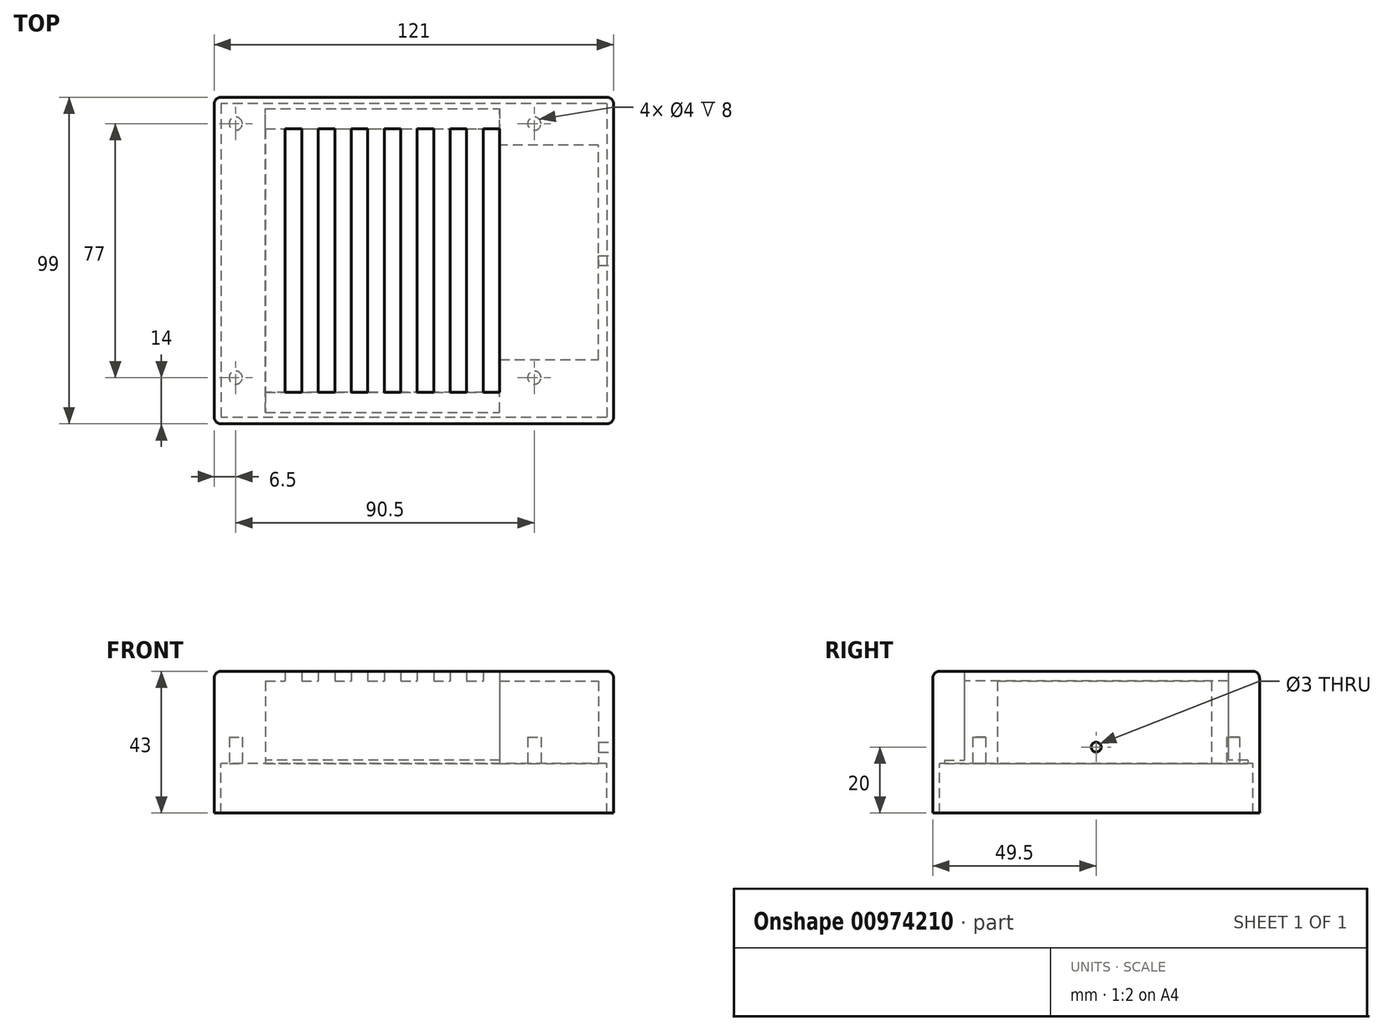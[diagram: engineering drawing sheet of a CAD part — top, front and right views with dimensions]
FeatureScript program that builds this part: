
annotation { "Feature Type Name" : "Feature", "Feature Type Description" : "" }
export const myFeature = defineFeature(function(context is Context, id is Id, definition is map)
    precondition{}
    {
        {
            var Q0;
            Q0=qCreatedBy(makeId("Top.planeOp"),FACE);
            var sketch = newSketch(context, id + "F0", { "sketchPlane" : qUnion([Q0])});
            skLineSegment(sketch, "E0.bottom", {"start": v(58.5, 47.5) * mm, "end": v(-58.5, 47.5) * mm});
            skLineSegment(sketch, "E0.top", {"start": v(58.5, -47.5) * mm, "end": v(-58.5, -47.5) * mm});
            skLineSegment(sketch, "E0.left", {"start": v(58.5, 47.5) * mm, "end": v(58.5, -47.5) * mm});
            skLineSegment(sketch, "E0.right", {"start": v(-58.5, 47.5) * mm, "end": v(-58.5, -47.5) * mm});
            skPoint(sketch, "E0.middle", {"position": v(0, 0) * mm});
            skLineSegment(sketch, "E1.bottom", {"start": v(60.5, 49.5) * mm, "end": v(-60.5, 49.5) * mm});
            skLineSegment(sketch, "E1.top", {"start": v(60.5, -49.5) * mm, "end": v(-60.5, -49.5) * mm});
            skLineSegment(sketch, "E1.left", {"start": v(60.5, 49.5) * mm, "end": v(60.5, -49.5) * mm});
            skLineSegment(sketch, "E1.right", {"start": v(-60.5, 49.5) * mm, "end": v(-60.5, -49.5) * mm});
            skSolve(sketch);
        }
        {
            var Q0;
            Q0=makeQuery(id+"F0.imprint","IMPRINT",FACE,{"disambiguationData":[TD([[makeQuery(id+"F0.imprint","IMPRINT",EDGE,{"derivedFrom":sQuery(id+"F0.wireOp",EDGE,"E0.bottom")}),-1.0]])]});
            extrude(context, id + "F1", {"entities" : qUnion([Q0]), "oppositeDirection" : true, "depth" : 15 * mm, "offsetDistance" : 25 * mm});
        }
        {
            var Q0;
            Q0=makeQuery(id+"F1.opExtrude","CAP_FACE",FACE,{"disambiguationData":[OSD([sQuery(id+"F0.wireOp",EDGE,"E0.bottom"),sQuery(id+"F0.wireOp",EDGE,"E0.top"),sQuery(id+"F0.wireOp",EDGE,"E0.left"),sQuery(id+"F0.wireOp",EDGE,"E0.right"),sQuery(id+"F0.wireOp",EDGE,"E1.bottom"),sQuery(id+"F0.wireOp",EDGE,"E1.top"),sQuery(id+"F0.wireOp",EDGE,"E1.left"),sQuery(id+"F0.wireOp",EDGE,"E1.right")])],"isStart":true});
            var sketch = newSketch(context, id + "F2", { "sketchPlane" : qUnion([Q0])});
            skLineSegment(sketch, "E2.bottom", {"start": v(35, 40) * mm, "end": v(-35, 40) * mm});
            skLineSegment(sketch, "E2.top", {"start": v(35, -40) * mm, "end": v(-35, -40) * mm});
            skLineSegment(sketch, "E2.left", {"start": v(35, 40) * mm, "end": v(35, -40) * mm, "construction": true});
            skLineSegment(sketch, "E2.right", {"start": v(-35, 40) * mm, "end": v(-35, -40) * mm, "construction": true});
            skPoint(sketch, "E2.middle", {"position": v(0, 0) * mm});
            skLineSegment(sketch, "E3.bottom", {"start": v(60.5, 49.5) * mm, "end": v(-60.5, 49.5) * mm});
            skLineSegment(sketch, "E3.top", {"start": v(60.5, -49.5) * mm, "end": v(-60.5, -49.5) * mm});
            skLineSegment(sketch, "E3.left", {"start": v(60.5, 49.5) * mm, "end": v(60.5, -49.5) * mm});
            skLineSegment(sketch, "E3.right", {"start": v(-60.5, 49.5) * mm, "end": v(-60.5, -49.5) * mm});
            skLineSegment(sketch, "E4", {"start": v(-35, -40) * mm, "end": v(-45, -40) * mm});
            skLineSegment(sketch, "E5", {"start": v(-45, -40) * mm, "end": v(-45, 40) * mm});
            skLineSegment(sketch, "E6", {"start": v(-45, 40) * mm, "end": v(-35, 40) * mm});
            skLineSegment(sketch, "E7", {"start": v(35, -40) * mm, "end": v(26, -40) * mm, "construction": true});
            skLineSegment(sketch, "E8", {"start": v(26, -40) * mm, "end": v(26, 40) * mm});
            skSolve(sketch);
        }
        {
            var Q0;
            Q0=qSketchRegion(id+"F2",true);
            extrude(context, id + "F3", {"entities" : qUnion([Q0]), "operationType" : NewBodyOperationType.ADD, "depth" : 28 * mm, "offsetDistance" : 25 * mm});
        }
        {
            var Q0;
            Q0=makeQuery(id+"F3.opExtrude","CAP_FACE",FACE,{"disambiguationData":[OSD([sQuery(id+"F2.wireOp",EDGE,"E2.bottom"),sQuery(id+"F2.wireOp",EDGE,"E2.top"),sQuery(id+"F2.wireOp",EDGE,"E2.left"),sQuery(id+"F2.wireOp",EDGE,"E2.right"),sQuery(id+"F2.wireOp",EDGE,"E3.bottom"),sQuery(id+"F2.wireOp",EDGE,"E3.top"),sQuery(id+"F2.wireOp",EDGE,"E3.left"),sQuery(id+"F2.wireOp",EDGE,"E3.right")])],"isStart":true});
            var sketch = newSketch(context, id + "F4", { "sketchPlane" : qUnion([Q0])});
            skLineSegment(sketch, "E9", {"start": v(-58.5, 47.5) * mm, "end": v(-58.5, 35.5) * mm, "construction": true});
            skLineSegment(sketch, "E10", {"start": v(-58.5, 35.5) * mm, "end": v(-54, 35.5) * mm, "construction": true});
            skCircle(sketch, "E11", {"center": v(-54, 35.5) * mm, "radius": 2 * mm});
            skLineSegment(sketch, "E12", {"start": v(-58.5, -47.5) * mm, "end": v(-58.5, -41.5) * mm, "construction": true});
            skLineSegment(sketch, "E13", {"start": v(-58.5, -41.5) * mm, "end": v(-54, -41.5) * mm, "construction": true});
            skCircle(sketch, "E14", {"center": v(-54, -41.5) * mm, "radius": 2 * mm});
            skLineSegment(sketch, "E15", {"start": v(58.5, 47.5) * mm, "end": v(58.5, 35.5) * mm, "construction": true});
            skLineSegment(sketch, "E16", {"start": v(58.5, 35.5) * mm, "end": v(36.5, 35.5) * mm, "construction": true});
            skCircle(sketch, "E17", {"center": v(36.5, 35.5) * mm, "radius": 2 * mm});
            skLineSegment(sketch, "E18", {"start": v(58.5, -47.5) * mm, "end": v(58.5, -41.5) * mm, "construction": true});
            skLineSegment(sketch, "E19", {"start": v(58.5, -41.5) * mm, "end": v(36.5, -41.5) * mm, "construction": true});
            skCircle(sketch, "E20", {"center": v(36.5, -41.5) * mm, "radius": 2 * mm});
            skSolve(sketch);
        }
        {
            var Q0;
            Q0 = qSketchRegion(id + "F4", true);
            extrude(context, id + "F5", {"entities" : qUnion([Q0]), "operationType" : NewBodyOperationType.REMOVE, "oppositeDirection" : true, "depth" : 8 * mm, "offsetDistance" : 25 * mm});
        }
        {
            var Q0;
            Q0=makeQuery(id+"F3.opExtrude","SWEPT_FACE",FACE,{"disambiguationData":[OSD([sQuery(id+"F2.wireOp",EDGE,"E2.top"),sQuery(id+"F2.wireOp",EDGE,"E4")])]});
            var sketch = newSketch(context, id + "F6", { "sketchPlane" : qUnion([Q0])});
            skLineSegment(sketch, "E21.bottom", {"start": v(45, 28) * mm, "end": v(39, 28) * mm});
            skLineSegment(sketch, "E21.top", {"start": v(45, 25) * mm, "end": v(39, 25) * mm});
            skLineSegment(sketch, "E21.left", {"start": v(45, 28) * mm, "end": v(45, 25) * mm});
            skLineSegment(sketch, "E21.right", {"start": v(39, 28) * mm, "end": v(39, 25) * mm});
            skLineSegment(sketch, "E22", {"start": v(39, 28) * mm, "end": v(34, 28) * mm, "construction": true});
            skLineSegment(sketch, "E23.bottom", {"start": v(34, 28) * mm, "end": v(29, 28) * mm});
            skLineSegment(sketch, "E23.top", {"start": v(34, 25) * mm, "end": v(29, 25) * mm});
            skLineSegment(sketch, "E23.left", {"start": v(34, 28) * mm, "end": v(34, 25) * mm});
            skLineSegment(sketch, "E23.right", {"start": v(29, 28) * mm, "end": v(29, 25) * mm});
            skLineSegment(sketch, "E24", {"start": v(29, 28) * mm, "end": v(24, 28) * mm, "construction": true});
            skLineSegment(sketch, "E25.bottom", {"start": v(24, 28) * mm, "end": v(19, 28) * mm});
            skLineSegment(sketch, "E25.top", {"start": v(24, 25) * mm, "end": v(19, 25) * mm});
            skLineSegment(sketch, "E25.left", {"start": v(24, 28) * mm, "end": v(24, 25) * mm});
            skLineSegment(sketch, "E25.right", {"start": v(19, 28) * mm, "end": v(19, 25) * mm});
            skLineSegment(sketch, "E26", {"start": v(19, 28) * mm, "end": v(14, 28) * mm, "construction": true});
            skLineSegment(sketch, "E27.bottom", {"start": v(14, 28) * mm, "end": v(9, 28) * mm});
            skLineSegment(sketch, "E27.top", {"start": v(14, 25) * mm, "end": v(9, 25) * mm});
            skLineSegment(sketch, "E27.left", {"start": v(14, 28) * mm, "end": v(14, 25) * mm});
            skLineSegment(sketch, "E27.right", {"start": v(9, 28) * mm, "end": v(9, 25) * mm});
            skLineSegment(sketch, "E28", {"start": v(9, 28) * mm, "end": v(4, 28) * mm, "construction": true});
            skLineSegment(sketch, "E29.bottom", {"start": v(4, 28) * mm, "end": v(-1, 28) * mm});
            skLineSegment(sketch, "E29.top", {"start": v(4, 25) * mm, "end": v(-1, 25) * mm});
            skLineSegment(sketch, "E29.left", {"start": v(4, 28) * mm, "end": v(4, 25) * mm});
            skLineSegment(sketch, "E29.right", {"start": v(-1, 28) * mm, "end": v(-1, 25) * mm});
            skLineSegment(sketch, "E30", {"start": v(-1, 28) * mm, "end": v(-6, 28) * mm, "construction": true});
            skLineSegment(sketch, "E31.bottom", {"start": v(-6, 28) * mm, "end": v(-11, 28) * mm});
            skLineSegment(sketch, "E31.top", {"start": v(-6, 25) * mm, "end": v(-11, 25) * mm});
            skLineSegment(sketch, "E31.left", {"start": v(-6, 28) * mm, "end": v(-6, 25) * mm});
            skLineSegment(sketch, "E31.right", {"start": v(-11, 28) * mm, "end": v(-11, 25) * mm});
            skLineSegment(sketch, "E32", {"start": v(-11, 28) * mm, "end": v(-16, 28) * mm, "construction": true});
            skLineSegment(sketch, "E33.bottom", {"start": v(-16, 28) * mm, "end": v(-21, 28) * mm});
            skLineSegment(sketch, "E33.top", {"start": v(-16, 25) * mm, "end": v(-21, 25) * mm});
            skLineSegment(sketch, "E33.left", {"start": v(-16, 28) * mm, "end": v(-16, 25) * mm});
            skLineSegment(sketch, "E33.right", {"start": v(-21, 28) * mm, "end": v(-21, 25) * mm});
            skSolve(sketch);
        }
        {
            var Q0;
            Q0 = qSketchRegion(id + "F6", true);
            extrude(context, id + "F7", {"entities" : qUnion([Q0]), "operationType" : NewBodyOperationType.ADD, "endBound" : BoundingType.UP_TO_NEXT, "depth" : 25 * mm, "offsetDistance" : 25 * mm});
        }
        {
            var Q0;
            Q0=makeQuery(id+"F3.opExtrude","CAP_FACE",FACE,{"disambiguationData":[OSD([sQuery(id+"F2.wireOp",EDGE,"E2.bottom"),sQuery(id+"F2.wireOp",EDGE,"E2.top"),sQuery(id+"F2.wireOp",EDGE,"E3.bottom"),sQuery(id+"F2.wireOp",EDGE,"E3.top"),sQuery(id+"F2.wireOp",EDGE,"E3.left"),sQuery(id+"F2.wireOp",EDGE,"E3.right"),sQuery(id+"F2.wireOp",EDGE,"E4"),sQuery(id+"F2.wireOp",EDGE,"E5"),sQuery(id+"F2.wireOp",EDGE,"E6"),sQuery(id+"F2.wireOp",EDGE,"E8")])],"isStart":true});
            var sketch = newSketch(context, id + "F8", { "sketchPlane" : qUnion([Q0])});
            skLineSegment(sketch, "E34", {"start": v(-45, 40) * mm, "end": v(-45, 46) * mm});
            skLineSegment(sketch, "E35", {"start": v(-45, 46) * mm, "end": v(26, 46) * mm});
            skLineSegment(sketch, "E36", {"start": v(26, 46) * mm, "end": v(26, 40) * mm});
            skLineSegment(sketch, "E37", {"start": v(26, 40) * mm, "end": v(-45, 40) * mm});
            skLineSegment(sketch, "E38", {"start": v(-45, -40) * mm, "end": v(-45, -46) * mm});
            skLineSegment(sketch, "E39", {"start": v(-45, -46) * mm, "end": v(26, -46) * mm});
            skLineSegment(sketch, "E40", {"start": v(26, -46) * mm, "end": v(26, -40) * mm});
            skLineSegment(sketch, "E41", {"start": v(26, -40) * mm, "end": v(-45, -40) * mm});
            skSolve(sketch);
        }
        {
            var Q0;
            Q0 = qSketchRegion(id + "F8", true);
            extrude(context, id + "F9", {"entities" : qUnion([Q0]), "operationType" : NewBodyOperationType.REMOVE, "oppositeDirection" : true, "depth" : 1 * mm, "offsetDistance" : 25 * mm});
        }
        {
            var Q0;
            Q0=makeQuery(id+"F3.opExtrude","CAP_FACE",FACE,{"disambiguationData":[OSD([sQuery(id+"F2.wireOp",EDGE,"E2.bottom"),sQuery(id+"F2.wireOp",EDGE,"E2.top"),sQuery(id+"F2.wireOp",EDGE,"E3.bottom"),sQuery(id+"F2.wireOp",EDGE,"E3.top"),sQuery(id+"F2.wireOp",EDGE,"E3.left"),sQuery(id+"F2.wireOp",EDGE,"E3.right"),sQuery(id+"F2.wireOp",EDGE,"E4"),sQuery(id+"F2.wireOp",EDGE,"E5"),sQuery(id+"F2.wireOp",EDGE,"E6"),sQuery(id+"F2.wireOp",EDGE,"E8")])],"isStart":true});
            var sketch = newSketch(context, id + "F10", { "sketchPlane" : qUnion([Q0])});
            skLineSegment(sketch, "E42.bottom", {"start": v(26, 0) * mm, "end": v(26, 0) * mm});
            skLineSegment(sketch, "E42.top", {"start": v(26, 30) * mm, "end": v(26, 30) * mm});
            skLineSegment(sketch, "E42.left", {"start": v(26, 0) * mm, "end": v(26, 30) * mm, "construction": true});
            skLineSegment(sketch, "E42.right", {"start": v(26, 0) * mm, "end": v(26, 30) * mm, "construction": true});
            skLineSegment(sketch, "E43", {"start": v(26, 0) * mm, "end": v(26, -35) * mm, "construction": true});
            skLineSegment(sketch, "E44", {"start": v(26, 30) * mm, "end": v(56, 30) * mm});
            skLineSegment(sketch, "E45", {"start": v(56, 30) * mm, "end": v(56, -35) * mm});
            skLineSegment(sketch, "E46", {"start": v(56, -35) * mm, "end": v(26, -35) * mm});
            skLineSegment(sketch, "E47", {"start": v(26, 30) * mm, "end": v(26, -35) * mm});
            skSolve(sketch);
        }
        {
            var Q0;
            Q0 = qSketchRegion(id + "F10", true);
            extrude(context, id + "F11", {"entities" : qUnion([Q0]), "operationType" : NewBodyOperationType.REMOVE, "oppositeDirection" : true, "depth" : 25 * mm, "offsetDistance" : 25 * mm});
        }
        {
            var Q0;
            Q0=makeQuery(id+"F3.boolean.opBoolean","MERGE",EDGE,{"derivedFrom":[makeQuery(id+"F1.opExtrude","SWEPT_EDGE",EDGE,{"disambiguationData":[OSD([sQuery(id+"F0.wireOp",EDGE,"E1.bottom"),sQuery(id+"F0.wireOp",EDGE,"E1.right")])]}),makeQuery(id+"F3.opExtrude","SWEPT_EDGE",EDGE,{"disambiguationData":[OSD([sQuery(id+"F2.wireOp",EDGE,"E3.bottom"),sQuery(id+"F2.wireOp",EDGE,"E3.right")])]})]});
            var Q1;
            Q1=makeQuery(id+"F3.opExtrude","CAP_EDGE",EDGE,{"disambiguationData":[OSD([sQuery(id+"F2.wireOp",EDGE,"E3.right")])],"isStart":false});
            var Q2;
            Q2=makeQuery(id+"F3.opExtrude","CAP_EDGE",EDGE,{"disambiguationData":[OSD([sQuery(id+"F2.wireOp",EDGE,"E3.bottom")])],"isStart":false});
            var Q3;
            Q3=makeQuery(id+"F3.boolean.opBoolean","MERGE",EDGE,{"derivedFrom":[makeQuery(id+"F1.opExtrude","SWEPT_EDGE",EDGE,{"disambiguationData":[OSD([sQuery(id+"F0.wireOp",EDGE,"E1.top"),sQuery(id+"F0.wireOp",EDGE,"E1.right")])]}),makeQuery(id+"F3.opExtrude","SWEPT_EDGE",EDGE,{"disambiguationData":[OSD([sQuery(id+"F2.wireOp",EDGE,"E3.top"),sQuery(id+"F2.wireOp",EDGE,"E3.right")])]})]});
            var Q4;
            Q4=makeQuery(id+"F3.opExtrude","CAP_EDGE",EDGE,{"disambiguationData":[OSD([sQuery(id+"F2.wireOp",EDGE,"E3.top")])],"isStart":false});
            var Q5;
            Q5=makeQuery(id+"F3.boolean.opBoolean","MERGE",EDGE,{"derivedFrom":[makeQuery(id+"F1.opExtrude","SWEPT_EDGE",EDGE,{"disambiguationData":[OSD([sQuery(id+"F0.wireOp",EDGE,"E1.top"),sQuery(id+"F0.wireOp",EDGE,"E1.left")])]}),makeQuery(id+"F3.opExtrude","SWEPT_EDGE",EDGE,{"disambiguationData":[OSD([sQuery(id+"F2.wireOp",EDGE,"E3.top"),sQuery(id+"F2.wireOp",EDGE,"E3.left")])]})]});
            var Q6;
            Q6=makeQuery(id+"F3.opExtrude","CAP_EDGE",EDGE,{"disambiguationData":[OSD([sQuery(id+"F2.wireOp",EDGE,"E3.left")])],"isStart":false});
            var Q7;
            Q7=makeQuery(id+"F3.boolean.opBoolean","MERGE",EDGE,{"derivedFrom":[makeQuery(id+"F1.opExtrude","SWEPT_EDGE",EDGE,{"disambiguationData":[OSD([sQuery(id+"F0.wireOp",EDGE,"E1.bottom"),sQuery(id+"F0.wireOp",EDGE,"E1.left")])]}),makeQuery(id+"F3.opExtrude","SWEPT_EDGE",EDGE,{"disambiguationData":[OSD([sQuery(id+"F2.wireOp",EDGE,"E3.bottom"),sQuery(id+"F2.wireOp",EDGE,"E3.left")])]})]});
            fillet(context, id + "F12", {"entities" : qUnion([Q0, Q1, Q2, Q3, Q4, Q5, Q6, Q7]), "radius" : 2 * mm, "tangentPropagation" : true, "allowEdgeOverflow" : false});
        }
        {
            var Q0;
            Q0=makeQuery(id+"F3.boolean.opBoolean","MERGE",FACE,{"derivedFrom":[makeQuery(id+"F1.opExtrude","SWEPT_FACE",FACE,{"disambiguationData":[OSD([sQuery(id+"F0.wireOp",EDGE,"E1.left")])]}),makeQuery(id+"F3.opExtrude","SWEPT_FACE",FACE,{"disambiguationData":[OSD([sQuery(id+"F2.wireOp",EDGE,"E3.left")])]})]});
            var sketch = newSketch(context, id + "F13", { "sketchPlane" : qUnion([Q0])});
            skLineSegment(sketch, "E48", {"start": v(0, -15) * mm, "end": v(0, 5) * mm, "construction": true});
            skCircle(sketch, "E49", {"center": v(0, 5) * mm, "radius": 1.5 * mm});
            skSolve(sketch);
        }
        {
            var Q0;
            Q0 = qSketchRegion(id + "F13", true);
            extrude(context, id + "F14", {"entities" : qUnion([Q0]), "operationType" : NewBodyOperationType.REMOVE, "endBound" : BoundingType.UP_TO_NEXT, "oppositeDirection" : true, "depth" : 25 * mm, "offsetDistance" : 25 * mm});
        }
    });
